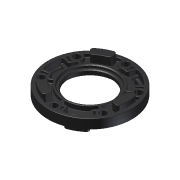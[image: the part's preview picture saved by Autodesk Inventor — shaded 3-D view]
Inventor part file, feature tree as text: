
AUTODESK INVENTOR PART (.ipt)
format: ipt  version: 2013 (Build 170138000, 138)  size: 1,764,352 bytes
history: native  units: in
note: dims shown in document units (in); Inventor stores cm internally (conversion verified against a paired STEP export)
features: fillet x1, other x1, imported_body x1
ambient origin geometry x8: Origin, YZ Plane, XZ Plane, XY Plane, X Axis, Y Axis, Z Axis, Center Point
feature tree (3):
  fillet  "Fillet10"  [1 undecoded]
  other  "217-3234-STEP1"
  imported_body  "Base1"
note: 1 required parameter value undecoded (feature->parameter linkage not recoverable at this tier; creation-order binding heuristic only, values carry confidence <= 0.55)
